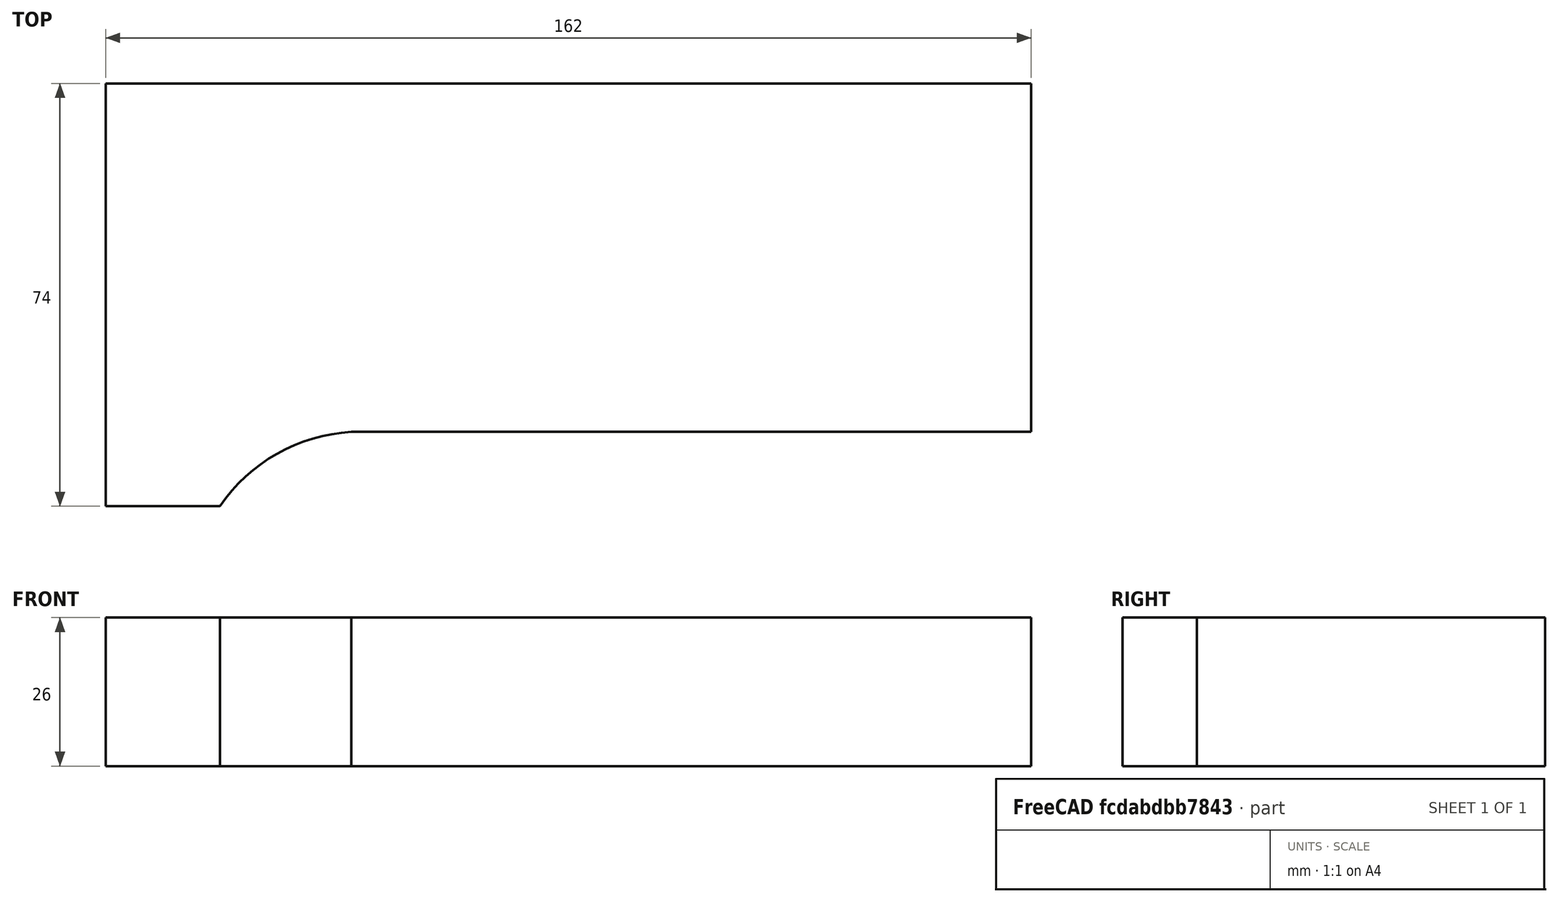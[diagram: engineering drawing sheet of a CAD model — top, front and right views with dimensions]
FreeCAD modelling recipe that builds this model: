
FCSTD DOCUMENT  (FreeCAD 0.20R29603 (Git))
Label: BlocLateralPanneauControle
License: All rights reserved
LicenseURL: http://en.wikipedia.org/wiki/All_rights_reserved
objects: TechDraw::DrawViewDimension×8, Sketcher::SketchObject×1, PartDesign::Pad×1, TechDraw::DrawSVGTemplate×1, TechDraw::DrawViewPart×1, TechDraw::DrawPage×1
note: 3 computed .brp shape members not serialized (recipe doc carries the construction recipe); baked Part::Feature solids carry a one-line shape summary decoded from their .brp

FEATURE [Sketcher::SketchObject] Sketch
  FullyConstrained = true
  MapMode = 5
  sketch-geometry (6):
    g0: LineSegment StartX=0 StartY=74 StartZ=0 EndX=162 EndY=74 EndZ=0
    g1: LineSegment StartX=0 StartY=0 StartZ=0 EndX=0 EndY=74 EndZ=0
    g2: ArcOfCircle CenterX=44.7536 CenterY=-16.9487 CenterZ=0 NormalX=0 NormalY=0 NormalZ=1 AngleXU=0 Radius=30 StartAngle=1.62928 EndAngle=2.54121
    g3: LineSegment StartX=43 StartY=13 StartZ=0 EndX=162 EndY=13 EndZ=0
    g4: LineSegment StartX=20 StartY=-2.888e-11 StartZ=0 EndX=0 EndY=0 EndZ=0
    g5: LineSegment StartX=162 StartY=74 StartZ=0 EndX=162 EndY=13 EndZ=0
  constraints (18):
    c: Coincident(g1,g0)
    c: Horizontal(g0)
    c: Vertical(g1)
    c: DistanceY(g1,g1) = 74
    c: DistanceX(g-1,g2) = 43
    c: DistanceX(g-1,g4) = 20
    c: DistanceY(g-1,g4) = 0
    c: DistanceY(g-1,g2) = 13
    c: Radius(g2) = 30
    c: Coincident(g3,g2)
    c: Coincident(g4,g-1)
    c: Coincident(g5,g3)
    c: Horizontal(g3)
    c: Coincident(g5,g0)
    c: DistanceX(g0,g0) = 162
    c: Vertical(g5)
    c: Coincident(g1,g-1)
    c: Coincident(g2,g4)
FEATURE [PartDesign::Pad] Pad
  AllowMultiFace = false
  Direction = (0,0,1)
  Length = 26
  Length2 = 100
  Profile = -> Sketch
  Refine = true
  Type = 0
FEATURE [TechDraw::DrawSVGTemplate] Template
  Height = 210
  Orientation = 1
  Width = 297
FEATURE [TechDraw::DrawViewPart] View
  CoarseView = false
  Direction = (0,0,1)
  Focus = 100
  HardHidden = false
  IsoCount = 0
  IsoHidden = false
  IsoVisible = false
  LockPosition = false
  Perspective = false
  Rotation = 0
  ScaleType = 0
  SeamHidden = false
  SeamVisible = false
  SmoothHidden = false
  SmoothVisible = false
  Source = -> [Pad]
  X = 148.5
  XDirection = (1,0,0)
  Y = 105
FEATURE [TechDraw::DrawViewDimension] Dimension
  AngleOverride = false
  Arbitrary = false
  ArbitraryTolerances = false
  EqualTolerance = false
  ExtensionAngle = 0
  FormatSpec = %.2f
  FormatSpecOverTolerance = %+.2f
  FormatSpecUnderTolerance = %+.2f
  Inverted = false
  LineAngle = 0
  LockPosition = false
  MeasureType = 1
  OverTolerance = 0
  References2D = -> [View]
  Rotation = 0
  ScaleType = 0
  TheoreticalExact = false
  Type = 1
  UnderTolerance = 0
  X = 4.44583
  Y = 55.0448
FEATURE [TechDraw::DrawViewDimension] Dimension001
  AngleOverride = false
  Arbitrary = false
  ArbitraryTolerances = false
  EqualTolerance = false
  ExtensionAngle = 0
  FormatSpec = %.2f
  FormatSpecOverTolerance = %+.2f
  FormatSpecUnderTolerance = %+.2f
  Inverted = false
  LineAngle = 0
  LockPosition = false
  MeasureType = 1
  OverTolerance = 0
  References2D = -> [View]
  Rotation = 0
  ScaleType = 0
  TheoreticalExact = false
  Type = 2
  UnderTolerance = 0
  X = -101.66
  Y = -2.61519
FEATURE [TechDraw::DrawViewDimension] Dimension002
  AngleOverride = false
  Arbitrary = false
  ArbitraryTolerances = false
  EqualTolerance = false
  ExtensionAngle = 0
  FormatSpec = %.2f
  FormatSpecOverTolerance = %+.2f
  FormatSpecUnderTolerance = %+.2f
  Inverted = false
  LineAngle = 0
  LockPosition = false
  MeasureType = 1
  OverTolerance = 0
  References2D = -> [View]
  Rotation = 0
  ScaleType = 0
  TheoreticalExact = false
  Type = 2
  UnderTolerance = 0
  X = 99.3064
  Y = 8.33063
FEATURE [TechDraw::DrawViewDimension] Dimension003
  AngleOverride = false
  Arbitrary = false
  ArbitraryTolerances = false
  EqualTolerance = false
  ExtensionAngle = 0
  FormatSpec = %.2f
  FormatSpecOverTolerance = %+.2f
  FormatSpecUnderTolerance = %+.2f
  Inverted = false
  LineAngle = 0
  LockPosition = false
  MeasureType = 1
  OverTolerance = 0
  References2D = -> [View]
  Rotation = 0
  ScaleType = 0
  TheoreticalExact = false
  Type = 1
  UnderTolerance = 0
  X = -71.2615
  Y = -55.0448
FEATURE [TechDraw::DrawViewDimension] Dimension004
  AngleOverride = false
  Arbitrary = false
  ArbitraryTolerances = false
  EqualTolerance = false
  ExtensionAngle = 0
  FormatSpec = %.2f
  FormatSpecOverTolerance = %+.2f
  FormatSpecUnderTolerance = %+.2f
  Inverted = false
  LineAngle = 0
  LockPosition = false
  MeasureType = 1
  OverTolerance = 0
  References2D = -> [View]
  Rotation = 0
  ScaleType = 0
  TheoreticalExact = false
  Type = 1
  UnderTolerance = 0
  X = 26.7304
  Y = -4.38605
FEATURE [TechDraw::DrawViewDimension] Dimension005
  AngleOverride = false
  Arbitrary = false
  ArbitraryTolerances = false
  EqualTolerance = false
  ExtensionAngle = 0
  FormatSpec = R%.2f
  FormatSpecOverTolerance = %+.2f
  FormatSpecUnderTolerance = %+.2f
  Inverted = false
  LineAngle = 0
  LockPosition = false
  MeasureType = 1
  OverTolerance = 0
  References2D = -> [View]
  Rotation = 0
  ScaleType = 0
  TheoreticalExact = false
  Type = 4
  UnderTolerance = 0
  X = -67.7335
  Y = -11.2453
FEATURE [TechDraw::DrawViewDimension] Dimension006
  AngleOverride = false
  Arbitrary = false
  ArbitraryTolerances = false
  EqualTolerance = false
  ExtensionAngle = 0
  FormatSpec = %.2f
  FormatSpecOverTolerance = %+.2f
  FormatSpecUnderTolerance = %+.2f
  Inverted = false
  LineAngle = 0
  LockPosition = false
  MeasureType = 1
  OverTolerance = 0
  References2D = -> [View]
  Rotation = 0
  ScaleType = 0
  TheoreticalExact = false
  Type = 2
  UnderTolerance = 0
  X = -50.5161
  Y = -70.8417
FEATURE [TechDraw::DrawViewDimension] Dimension007
  AngleOverride = false
  Arbitrary = false
  ArbitraryTolerances = false
  EqualTolerance = false
  ExtensionAngle = 0
  FormatSpec = %.2f
  FormatSpecOverTolerance = %+.2f
  FormatSpecUnderTolerance = %+.2f
  Inverted = false
  LineAngle = 0
  LockPosition = false
  MeasureType = 1
  OverTolerance = 0
  References2D = -> [View]
  Rotation = 0
  ScaleType = 0
  TheoreticalExact = false
  Type = 1
  UnderTolerance = 0
  X = 22.3768
  Y = -38.9744
FEATURE [TechDraw::DrawPage] Page
  KeepUpdated = true
  NextBalloonIndex = 1
  ProjectionType = 0
  Template = -> Template
  Views = -> [View,Dimension,Dimension001,Dimension002,Dimension003,Dimension004,Dimension005,Dimension006,Dimension007]
